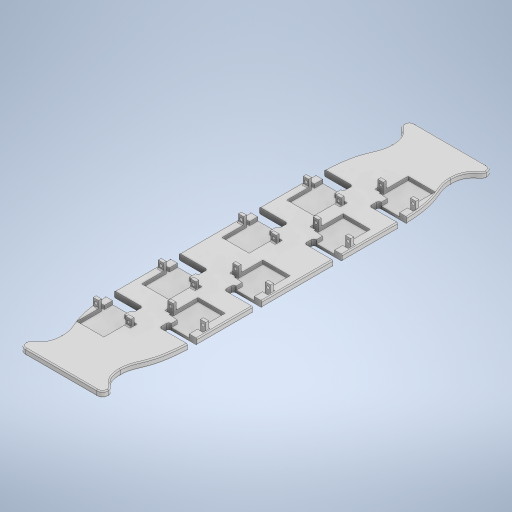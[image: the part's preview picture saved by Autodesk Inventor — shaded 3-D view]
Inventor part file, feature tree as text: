
AUTODESK INVENTOR PART (.ipt)
format: ipt  version: 2023.1 (Build 271208000, 208)  size: 910,848 bytes
history: native  units: mm
features: extrude x6, fillet x6, sketch x3, other x2
ambient origin geometry x8: Origin, YZ Plane, XZ Plane, XY Plane, X Axis, Y Axis, Z Axis, Center Point
bodies: Solid1 (feature_tree)
feature tree (17):
  extrude  "Baseplate"  Depth=250.0mm
  other  "Servo Feature Layout"
  extrude  "Horn Clearance Slot"  Depth=5.0mm
  extrude  "Servo Mount Pockets"  Depth=1.0mm
  fillet  "Fillets (Baseplate)"  Radius=55.0mm
  fillet  "Fillets (Clearance Slot)"  Radius=8.0mm
  extrude  "Extrusion6"  Depth=1.0mm
  extrude  "Extrusion7"  Depth=1.0mm
  extrude  "Extrusion8"  Depth=4.55mm
  fillet  "Fillet3"  Radius=2.4mm
  fillet  "Fillet4"  Radius=21.0mm
  fillet  "Fillet6"  Radius=10.0mm
  fillet  "Fillet7"  Radius=23.0mm
  other  "Baseplate Profile"
  sketch  "Sketch5"  dims[d8=70.0mm d9=250.0mm]
  sketch  "Sketch6"  dims[d16=5.0mm d17=0.0mm d18=34.0mm]
  sketch  "Sketch7"  dims[d19=55.0mm d20=34.0mm d21=55.0mm d23=8.0mm d24=29.8mm d25=7.0mm d26=4.55mm d27=2.4mm d28=21.0mm d30=10.0mm d31=23.0mm d38=4.55mm d39=4.55mm d40=1.1mm d41=2.44mm d42=15.3mm d43=5.2mm d44=16.563016mm d46=8.0mm d47=29.8mm d48=7.0mm d49=4.55mm d50=2.4mm d51=21.0mm d52=10.0mm d53=23.0mm d54=4.55mm d55=4.55mm d56=1.1mm d57=2.44mm d58=15.3mm d59=5.2mm d60=16.563016mm d61=8.0mm d62=29.8mm d63=7.0mm d64=4.55mm d65=2.4mm d66=21.0mm d67=10.0mm d68=23.0mm d69=4.55mm d70=4.55mm d71=1.1mm d72=2.44mm d73=15.3mm d74=5.2mm d75=16.563016mm d76=8.0mm d77=29.8mm d78=7.0mm d79=4.55mm d80=2.4mm d81=21.0mm d82=10.0mm d83=23.0mm d84=4.55mm d85=4.55mm d86=1.1mm d87=2.44mm d88=15.3mm d89=5.2mm d90=16.563016mm d91=24.0mm d93=5.0mm d94=0.0mm d95=3.0mm d96=0.0mm d97=30.0mm d99=40.0mm d110=5.0mm d111=5.0mm d112=25.0mm d113=35.0mm d114=10.0mm d115=10.0mm d116=5.0mm d117=0.9mm d118=2.0mm d126=2.5mm d128=2.5mm d129=2.5mm d130=2.5mm d131=2.5mm d132=2.5mm d133=2.5mm d134=2.5mm d135=6.0mm d136=0.0mm d137=3.0mm d138=3.0mm d139=2.5mm d140=2.5mm d141=6.0mm d142=0.0mm d143=3.0mm d144=3.0mm d145=2.5mm d146=2.5mm d147=10.0mm d148=0.0mm d149=1.0mm d150=0.1mm d151=1.0mm d152=0.1mm d154=1.0mm d155=1.0mm d153=0.5mm d156=0.872665mm]
